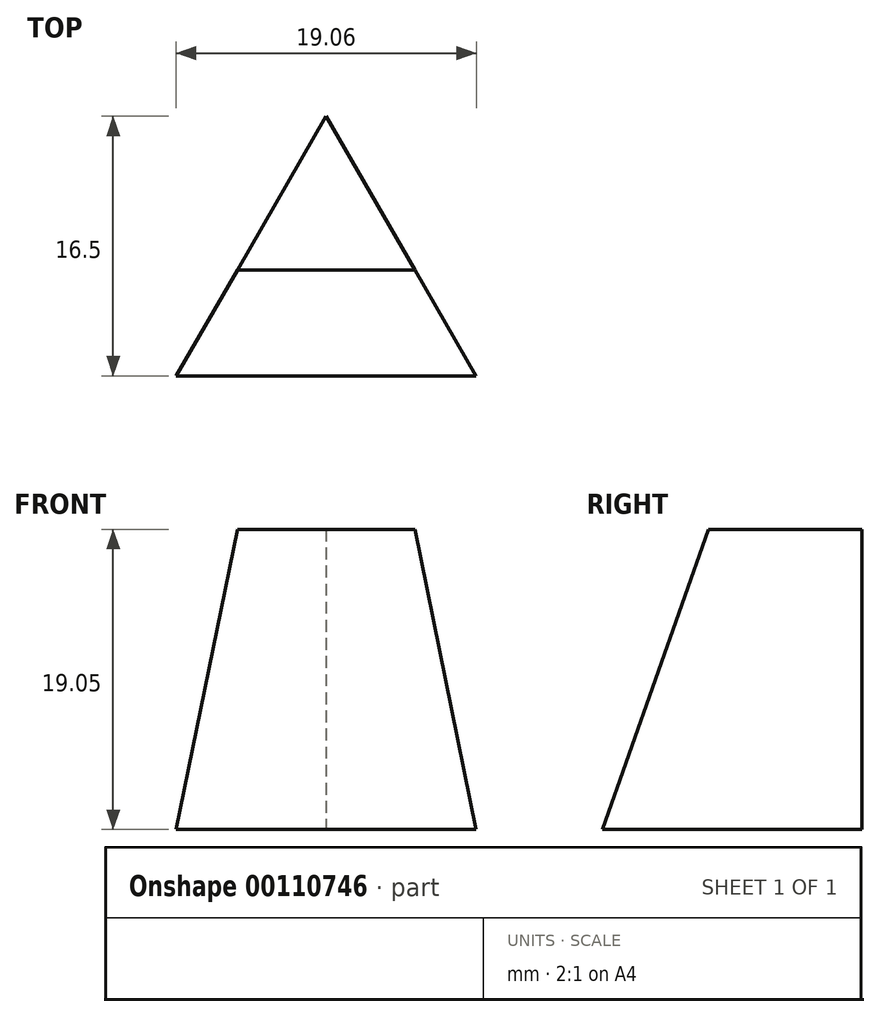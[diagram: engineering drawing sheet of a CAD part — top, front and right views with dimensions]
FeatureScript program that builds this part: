
annotation { "Feature Type Name" : "Feature", "Feature Type Description" : "" }
export const myFeature = defineFeature(function(context is Context, id is Id, definition is map)
    precondition{}
    {
        {
            var Q0;
            Q0=qCreatedBy(makeId("Top.planeOp"),FACE);
            var sketch = newSketch(context, id + "F0", { "sketchPlane" : qUnion([Q0])});
            skLineSegment(sketch, "E0", {"start": v(9.52, -5.5) * mm, "end": v(-9.52, -5.5) * mm});
            skLineSegment(sketch, "E1", {"start": v(-9.52, -5.5) * mm, "end": v(0, 11) * mm});
            skLineSegment(sketch, "E2", {"start": v(0, 11) * mm, "end": v(9.53, -5.5) * mm});
            skLineSegment(sketch, "E3", {"start": v(0, -5.5) * mm, "end": v(0, 0) * mm, "construction": true});
            skLineSegment(sketch, "E4", {"start": v(-4.76, 2.75) * mm, "end": v(0, 0) * mm, "construction": true});
            skLineSegment(sketch, "E5", {"start": v(4.76, 2.75) * mm, "end": v(0, 0) * mm, "construction": true});
            skSolve(sketch);
        }
        {
            var Q0;
            Q0=makeQuery(id+"F0.imprint","IMPRINT",FACE,{"disambiguationData":[TD([[makeQuery(id+"F0.imprint","IMPRINT",EDGE,{"derivedFrom":sQuery(id+"F0.wireOp",EDGE,"E0")}),-1.0]])]});
            extrude(context, id + "F1", {"entities" : qUnion([Q0]), "depth" : 19.05 * mm});
        }
        {
            var Q0;
            Q0=qCreatedBy(makeId("Right.planeOp"),FACE);
            var sketch = newSketch(context, id + "F2", { "sketchPlane" : qUnion([Q0])});
            skLineSegment(sketch, "E6", {"start": v(0, -2) * mm, "end": v(0, 21.26) * mm, "construction": true});
            skSolve(sketch);
        }
        {
            var Q0;
            Q0=qCreatedBy(makeId("Right.planeOp"),FACE);
            var sketch = newSketch(context, id + "F3", { "sketchPlane" : qUnion([Q0])});
            skLineSegment(sketch, "E7", {"start": v(-5.5, 0) * mm, "end": v(1.24, 19.05) * mm});
            skLineSegment(sketch, "E8.0", {"start": v(1.24, 19.05) * mm, "end": v(-5.5, 19.05) * mm});
            skLineSegment(sketch, "E8.1", {"start": v(-5.5, 19.05) * mm, "end": v(-5.5, 0) * mm});
            skPoint(sketch, "E9.orphan", {"position": v(11, 19.05) * mm});
            skPoint(sketch, "E10", {"position": v(0, 15.55) * mm});
            skCircle(sketch, "E11", {"center": v(0, 3.89) * mm, "radius": 3.89 * mm, "construction": true});
            skSolve(sketch);
        }
        {
            var Q0;
            Q0=qSketchRegion(id+"F3",true);
            extrude(context, id + "F4", {"entities" : qUnion([Q0]), "operationType" : NewBodyOperationType.REMOVE, "endBound" : BoundingType.THROUGH_ALL, "oppositeDirection" : true, "depth" : 25.4 * mm, "hasSecondDirection" : true, "secondDirectionBound" : SecondDirectionBoundingType.THROUGH_ALL, "secondDirectionOppositeDirection" : false, "secondDirectionDepth" : 25.4 * mm});
        }
    });
